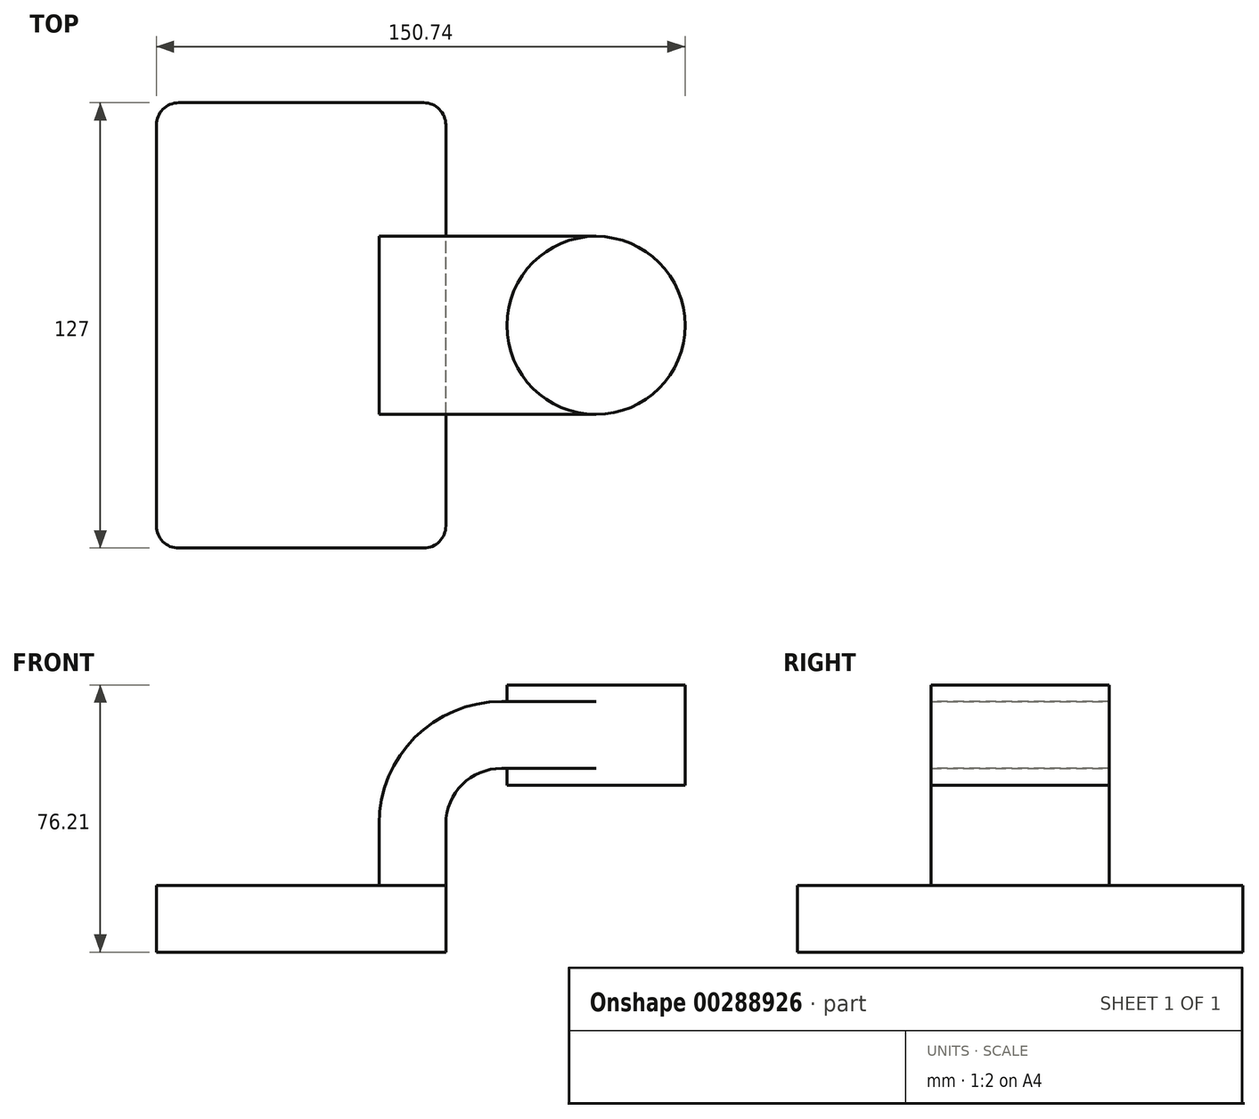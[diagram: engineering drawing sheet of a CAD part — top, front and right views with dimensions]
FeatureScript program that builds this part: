
annotation { "Feature Type Name" : "Feature", "Feature Type Description" : "" }
export const myFeature = defineFeature(function(context is Context, id is Id, definition is map)
    precondition{}
    {
        {
            var Q0;
            Q0=qCreatedBy(makeId("Front.planeOp"),FACE);
            var sketch = newSketch(context, id + "F0", { "sketchPlane" : qUnion([Q0])});
            skLineSegment(sketch, "E0.bottom", {"start": v(41.28, -9.52) * mm, "end": v(-41.28, -9.53) * mm});
            skLineSegment(sketch, "E0.top", {"start": v(41.27, 9.53) * mm, "end": v(-41.28, 9.53) * mm});
            skLineSegment(sketch, "E0.left", {"start": v(41.28, -9.52) * mm, "end": v(41.28, 9.53) * mm});
            skLineSegment(sketch, "E0.right", {"start": v(-41.28, -9.52) * mm, "end": v(-41.28, 9.53) * mm});
            skPoint(sketch, "E0.middle", {"position": v(0, 0) * mm});
            skLineSegment(sketch, "E1.bottom", {"start": v(58.67, 38.1) * mm, "end": v(109.47, 38.1) * mm});
            skLineSegment(sketch, "E1.top", {"start": v(58.67, 66.68) * mm, "end": v(109.47, 66.68) * mm});
            skLineSegment(sketch, "E1.left", {"start": v(58.67, 38.1) * mm, "end": v(58.67, 66.68) * mm});
            skLineSegment(sketch, "E1.right", {"start": v(109.47, 38.1) * mm, "end": v(109.47, 66.68) * mm});
            skPoint(sketch, "E1.middle", {"position": v(84.07, 52.39) * mm});
            skLineSegment(sketch, "E2", {"start": v(41.27, 9.53) * mm, "end": v(41.27, 27) * mm});
            skArc(sketch, "E3", {"start": v(41.27, 27) * mm, "mid": v(45.92, 38.23) * mm, "end": v(57.15, 42.88) * mm});
            skLineSegment(sketch, "E4", {"start": v(57.15, 42.88) * mm, "end": v(85.73, 42.88) * mm});
            skLineSegment(sketch, "E5.0", {"start": v(57.15, 61.93) * mm, "end": v(84.07, 61.93) * mm});
            skArc(sketch, "E5.1", {"start": v(22.23, 27) * mm, "mid": v(32.45, 51.7) * mm, "end": v(57.15, 61.93) * mm});
            skLineSegment(sketch, "E5.2", {"start": v(22.22, 9.53) * mm, "end": v(22.22, 27) * mm});
            skLineSegment(sketch, "E6", {"start": v(84.07, 61.93) * mm, "end": v(84.07, 38.1) * mm});
            skLineSegment(sketch, "E7", {"start": v(84.07, 61.93) * mm, "end": v(84.07, 66.68) * mm});
            skPoint(sketch, "E7.endSnap0", {"position": v(84.07, 66.68) * mm});
            skFitSpline(sketch, "E8", {"points": [v(-41.28, 9.53) * mm, v(57.15, 61.93) * mm], "startDerivative": vector(1.3, 121.87) * mm, "endDerivative": vector(104.29, -1.93) * mm});
            skSolve(sketch);
        }
        {
            var Q0;
            Q0=makeQuery(id+"F0.imprint","IMPRINT",FACE,{"disambiguationData":[TD([[makeQuery(id+"F0.imprint","IMPRINT",EDGE,{"derivedFrom":sQuery(id+"F0.wireOp",EDGE,"E0.bottom")}),-1.0]])]});
            extrude(context, id + "F1", {"entities" : qUnion([Q0]), "endBound" : BoundingType.SYMMETRIC, "depth" : 127 * mm});
        }
        {
            var Q0;
            {var subQ1=sQuery(id+"F0.wireOp",EDGE,"E2");Q0=makeQuery(id+"F0.imprint","IMPRINT",FACE,{"disambiguationData":[TD([[makeQuery(id+"F0.imprint","IMPRINT",EDGE,{"derivedFrom":subQ1}),1.0]])]});}
            var Q1;
            {var subQ0=sQuery(id+"F0.wireOp",EDGE,"E4");var subQ1=sQuery(id+"F0.wireOp",EDGE,"E1.left");var subQ2=makeQuery(id+"F0.imprint","INTERSECT",VERTEX,{"derivedFrom":[subQ1,subQ0]});Q1=makeQuery(id+"F0.imprint","IMPRINT",FACE,{"disambiguationData":[TD([[makeQuery(id+"F0.imprint","IMPRINT",EDGE,{"disambiguationData":[TD([[subQ2,-1.0]])],"derivedFrom":subQ1}),-1.0]])]});}
            extrude(context, id + "F2", {"entities" : qUnion([Q0, Q1]), "endBound" : BoundingType.SYMMETRIC, "depth" : 50.8 * mm});
        }
        {
            var Q0;
            Q0=makeQuery(id+"F0.imprint","IMPRINT",FACE,{"disambiguationData":[TD([[makeQuery(id+"F0.imprint","IMPRINT",EDGE,{"derivedFrom":sQuery(id+"F0.wireOp",EDGE,"E5.1")}),1.0]])]});
            extrude(context, id + "F3", {"entities" : qUnion([Q0]), "endBound" : BoundingType.SYMMETRIC, "depth" : 15.88 * mm});
        }
        {
            var Q0;
            {var subQ0=sQuery(id+"F0.wireOp",EDGE,"E1.right");Q0=makeQuery(id+"F0.imprint","IMPRINT",FACE,{"disambiguationData":[TD([[makeQuery(id+"F0.imprint","IMPRINT",EDGE,{"derivedFrom":subQ0}),1.0]])]});}
            var Q1;
            Q1=sQuery(id+"F0.wireOp",EDGE,"E6");
            revolve(context, id + "F4", {"operationType" : NewBodyOperationType.ADD, "entities" : qUnion([Q0]), "axis" : qUnion([Q1]), "revolveType" : RevolveType.FULL});
        }
        {
            var Q0;
            Q0=makeQuery(id+"F1.opExtrude","CAP_EDGE",EDGE,{"disambiguationData":[OSD([sQuery(id+"F0.wireOp",EDGE,"E0.left")])],"isStart":false});
            var Q1;
            Q1=makeQuery(id+"F1.opExtrude","CAP_EDGE",EDGE,{"disambiguationData":[OSD([sQuery(id+"F0.wireOp",EDGE,"E0.right")])],"isStart":false});
            var Q2;
            Q2=makeQuery(id+"F1.opExtrude","CAP_EDGE",EDGE,{"disambiguationData":[OSD([sQuery(id+"F0.wireOp",EDGE,"E0.left")])],"isStart":true});
            var Q3;
            Q3=makeQuery(id+"F1.opExtrude","CAP_EDGE",EDGE,{"disambiguationData":[OSD([sQuery(id+"F0.wireOp",EDGE,"E0.right")])],"isStart":true});
            fillet(context, id + "F5", {"entities" : qUnion([Q0, Q1, Q2, Q3]), "radius" : 6.35 * mm, "tangentPropagation" : true, "allowEdgeOverflow" : false});
        }
    });
